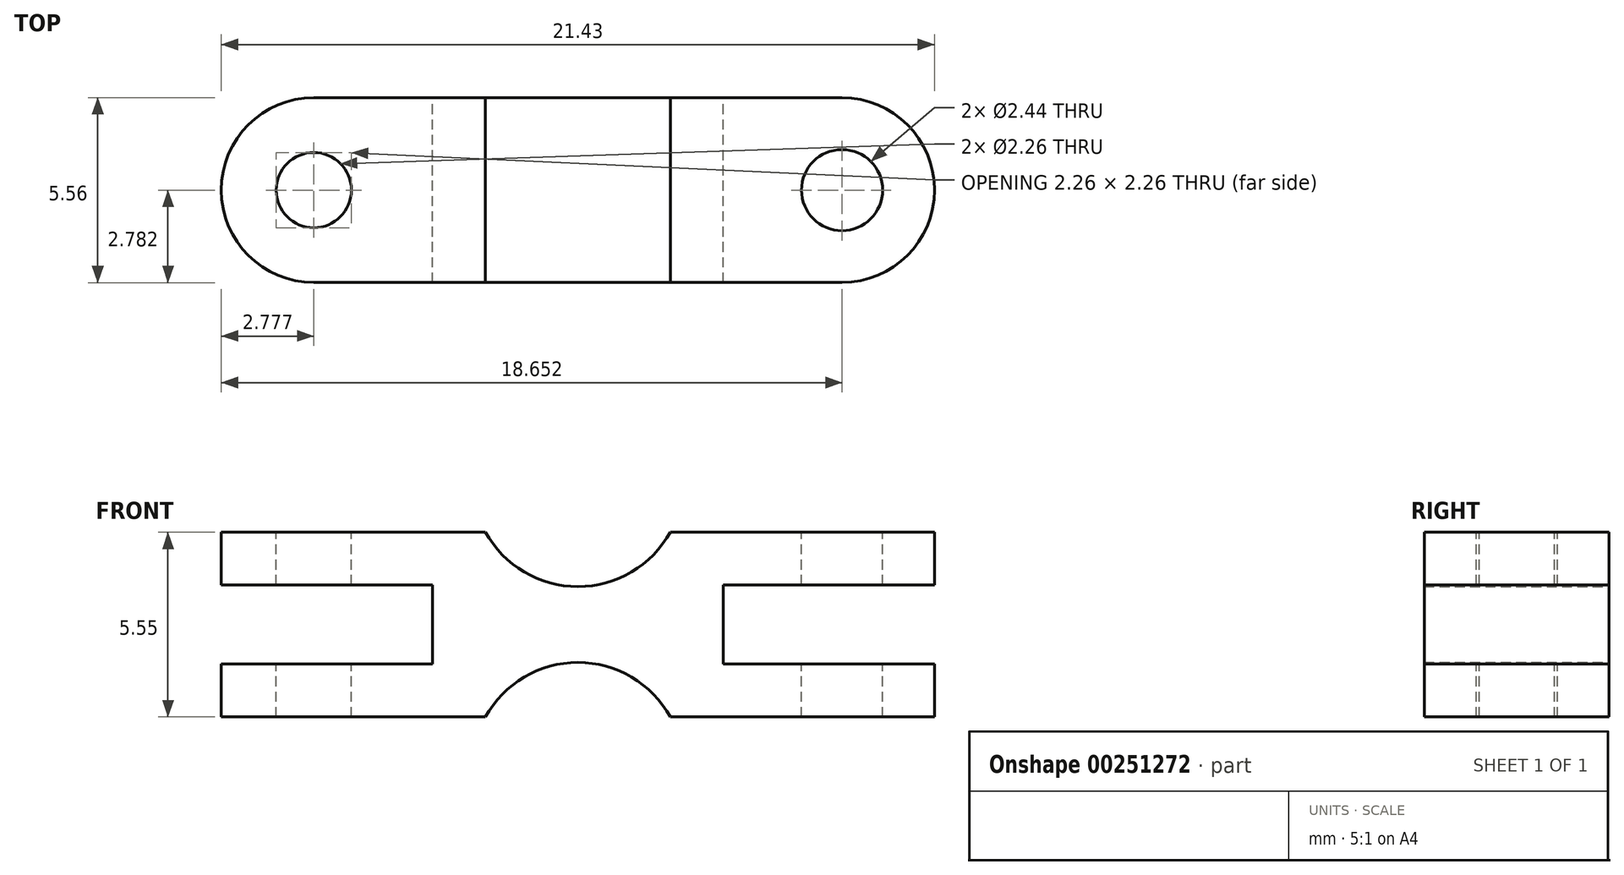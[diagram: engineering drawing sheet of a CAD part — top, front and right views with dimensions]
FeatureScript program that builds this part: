
annotation { "Feature Type Name" : "Feature", "Feature Type Description" : "" }
export const myFeature = defineFeature(function(context is Context, id is Id, definition is map)
    precondition{}
    {
        {
            var Q0;
            Q0=qCreatedBy(makeId("Front.planeOp"),FACE);
            var sketch = newSketch(context, id + "F0", { "sketchPlane" : qUnion([Q0])});
            skLineSegment(sketch, "E0", {"start": v(19.5, 28.35) * mm, "end": v(27.45, 28.35) * mm});
            skLineSegment(sketch, "E1", {"start": v(27.45, 28.35) * mm, "end": v(27.45, 22.8) * mm});
            skLineSegment(sketch, "E2", {"start": v(27.45, 22.8) * mm, "end": v(19.5, 22.8) * mm});
            skLineSegment(sketch, "E3", {"start": v(19.5, 22.8) * mm, "end": v(19.5, 24.39) * mm});
            skLineSegment(sketch, "E4", {"start": v(19.5, 24.39) * mm, "end": v(25.86, 24.39) * mm});
            skLineSegment(sketch, "E5", {"start": v(25.86, 24.39) * mm, "end": v(25.86, 26.77) * mm});
            skLineSegment(sketch, "E6", {"start": v(25.86, 26.77) * mm, "end": v(19.5, 26.77) * mm});
            skLineSegment(sketch, "E7", {"start": v(19.5, 26.77) * mm, "end": v(19.5, 28.35) * mm});
            skArc(sketch, "E8", {"start": v(27.45, 28.35) * mm, "mid": v(30.22, 26.72) * mm, "end": v(33, 28.35) * mm});
            skArc(sketch, "E9", {"start": v(33, 22.8) * mm, "mid": v(30.22, 24.44) * mm, "end": v(27.45, 22.8) * mm});
            skLineSegment(sketch, "E10", {"start": v(33, 28.35) * mm, "end": v(33, 22.8) * mm});
            skLineSegment(sketch, "E11", {"start": v(33, 22.8) * mm, "end": v(40.94, 22.8) * mm});
            skLineSegment(sketch, "E12", {"start": v(40.94, 22.8) * mm, "end": v(40.94, 24.39) * mm});
            skLineSegment(sketch, "E13", {"start": v(34.59, 24.39) * mm, "end": v(34.59, 26.77) * mm});
            skLineSegment(sketch, "E14", {"start": v(34.59, 26.77) * mm, "end": v(40.94, 26.77) * mm});
            skLineSegment(sketch, "E15", {"start": v(40.94, 26.77) * mm, "end": v(40.94, 28.35) * mm});
            skLineSegment(sketch, "E16", {"start": v(40.94, 28.35) * mm, "end": v(33, 28.35) * mm});
            skLineSegment(sketch, "E17", {"start": v(34.59, 24.39) * mm, "end": v(40.94, 24.39) * mm});
            skSolve(sketch);
        }
        {
            var Q0;
            Q0 = qSketchRegion(id + "F0", true);
            extrude(context, id + "F1", {"entities" : qUnion([Q0]), "depth" : 5.56 * mm});
        }
        {
            var Q0;
            Q0=makeQuery(id+"F1.opExtrude","SWEPT_FACE",FACE,{"disambiguationData":[OSD([sQuery(id+"F0.wireOp",EDGE,"E0")])]});
            var sketch = newSketch(context, id + "F2", { "sketchPlane" : qUnion([Q0])});
            skCircle(sketch, "E18", {"center": v(22.29, -2.78) * mm, "radius": 1.13 * mm});
            skCircle(sketch, "E19", {"center": v(38.16, -2.78) * mm, "radius": 1.22 * mm});
            skSolve(sketch);
        }
        {
            var Q0;
            Q0 = qSketchRegion(id + "F2", true);
            extrude(context, id + "F3", {"entities" : qUnion([Q0]), "operationType" : NewBodyOperationType.REMOVE, "oppositeDirection" : true, "depth" : 25.4 * mm});
        }
        {
            var Q0;
            Q0=makeQuery(id+"F1.opExtrude","CAP_EDGE",EDGE,{"disambiguationData":[OSD([sQuery(id+"F0.wireOp",EDGE,"E3")])],"isStart":true});
            var Q1;
            Q1=makeQuery(id+"F1.opExtrude","CAP_EDGE",EDGE,{"disambiguationData":[OSD([sQuery(id+"F0.wireOp",EDGE,"E7")])],"isStart":true});
            var Q2;
            Q2=makeQuery(id+"F1.opExtrude","CAP_EDGE",EDGE,{"disambiguationData":[OSD([sQuery(id+"F0.wireOp",EDGE,"E7")])],"isStart":false});
            var Q3;
            Q3=makeQuery(id+"F1.opExtrude","CAP_EDGE",EDGE,{"disambiguationData":[OSD([sQuery(id+"F0.wireOp",EDGE,"E3")])],"isStart":false});
            var Q4;
            Q4=makeQuery(id+"F1.opExtrude","CAP_EDGE",EDGE,{"disambiguationData":[OSD([sQuery(id+"F0.wireOp",EDGE,"E12")])],"isStart":true});
            var Q5;
            Q5=makeQuery(id+"F1.opExtrude","CAP_EDGE",EDGE,{"disambiguationData":[OSD([sQuery(id+"F0.wireOp",EDGE,"E15")])],"isStart":true});
            var Q6;
            Q6=makeQuery(id+"F1.opExtrude","CAP_EDGE",EDGE,{"disambiguationData":[OSD([sQuery(id+"F0.wireOp",EDGE,"E12")])],"isStart":false});
            var Q7;
            Q7=makeQuery(id+"F1.opExtrude","CAP_EDGE",EDGE,{"disambiguationData":[OSD([sQuery(id+"F0.wireOp",EDGE,"E15")])],"isStart":false});
            fillet(context, id + "F4", {"entities" : qUnion([Q0, Q1, Q2, Q3, Q4, Q5, Q6, Q7]), "radius" : 2.78 * mm, "tangentPropagation" : true, "allowEdgeOverflow" : false});
        }
    });
